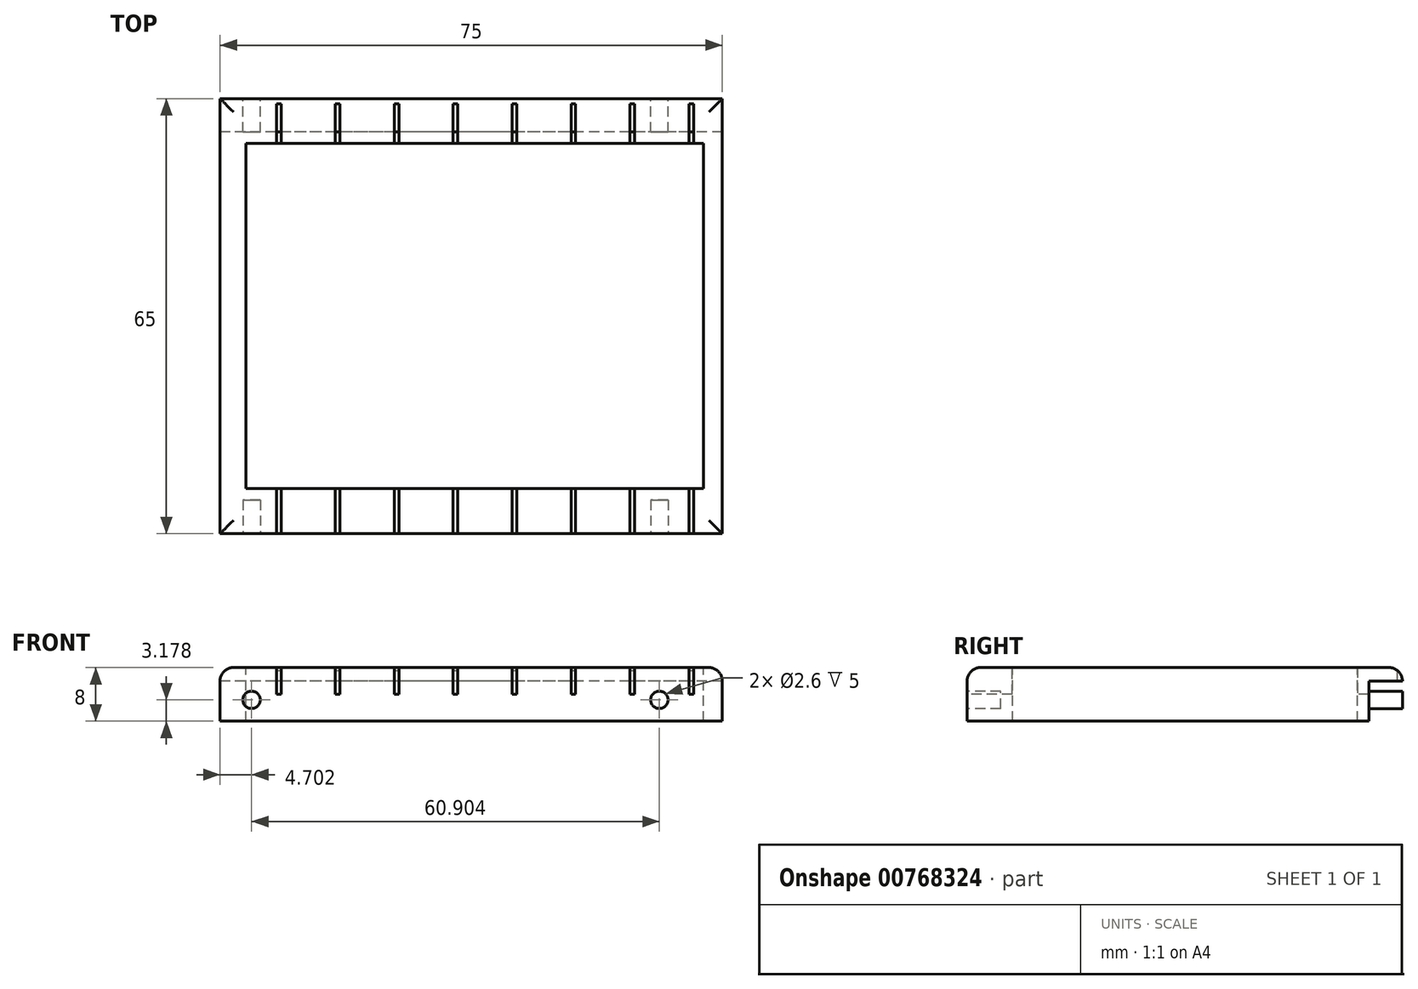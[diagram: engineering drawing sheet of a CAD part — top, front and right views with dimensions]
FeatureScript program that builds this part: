
annotation { "Feature Type Name" : "Feature", "Feature Type Description" : "" }
export const myFeature = defineFeature(function(context is Context, id is Id, definition is map)
    precondition{}
    {
        {
            var Q0;
            Q0=qCreatedBy(makeId("Top.planeOp"),FACE);
            var sketch = newSketch(context, id + "F0", { "sketchPlane" : qUnion([Q0])});
            skLineSegment(sketch, "E0.bottom", {"start": v(37.5, -32.5) * mm, "end": v(-37.5, -32.5) * mm});
            skLineSegment(sketch, "E0.top", {"start": v(37.5, 32.5) * mm, "end": v(-37.5, 32.5) * mm});
            skLineSegment(sketch, "E0.left", {"start": v(37.5, -32.5) * mm, "end": v(37.5, 32.5) * mm});
            skLineSegment(sketch, "E0.right", {"start": v(-37.5, -32.5) * mm, "end": v(-37.5, 32.5) * mm});
            skPoint(sketch, "E0.middle", {"position": v(0, 0) * mm});
            skSolve(sketch);
        }
        {
            var Q0;
            Q0=makeQuery(id+"F0.imprint","IMPRINT",FACE,{"disambiguationData":[TD([[makeQuery(id+"F0.imprint","IMPRINT",EDGE,{"derivedFrom":sQuery(id+"F0.wireOp",EDGE,"E0.bottom")}),-1.0]])]});
            extrude(context, id + "F1", {"entities" : qUnion([Q0]), "depth" : 8 * mm, "offsetDistance" : 25 * mm});
        }
        {
            var Q0;
            Q0=makeQuery(id+"F1.opExtrude","CAP_FACE",FACE,{"disambiguationData":[OSD([sQuery(id+"F0.wireOp",EDGE,"E0.bottom"),sQuery(id+"F0.wireOp",EDGE,"E0.top"),sQuery(id+"F0.wireOp",EDGE,"E0.left"),sQuery(id+"F0.wireOp",EDGE,"E0.right")])],"isStart":false});
            fillet(context, id + "F2", {"entities" : qUnion([Q0]), "radius" : 2 * mm, "tangentPropagation" : true, "allowEdgeOverflow" : false});
        }
        {
            var Q0;
            Q0=makeQuery(id+"F1.opExtrude","CAP_FACE",FACE,{"disambiguationData":[OSD([sQuery(id+"F0.wireOp",EDGE,"E0.bottom"),sQuery(id+"F0.wireOp",EDGE,"E0.top"),sQuery(id+"F0.wireOp",EDGE,"E0.left"),sQuery(id+"F0.wireOp",EDGE,"E0.right")])],"isStart":false});
            var sketch = newSketch(context, id + "F3", { "sketchPlane" : qUnion([Q0])});
            skLineSegment(sketch, "E1.bottom", {"start": v(-33.66, 25.81) * mm, "end": v(34.67, 25.81) * mm});
            skLineSegment(sketch, "E1.top", {"start": v(-33.66, -25.73) * mm, "end": v(34.67, -25.73) * mm});
            skLineSegment(sketch, "E1.left", {"start": v(-33.66, 25.81) * mm, "end": v(-33.66, -25.73) * mm});
            skLineSegment(sketch, "E1.right", {"start": v(34.67, 25.81) * mm, "end": v(34.67, -25.73) * mm});
            skSolve(sketch);
        }
        {
            var Q0;
            Q0=makeQuery(id+"F3.imprint","IMPRINT",FACE,{"disambiguationData":[TD([[makeQuery(id+"F3.imprint","IMPRINT",EDGE,{"derivedFrom":sQuery(id+"F3.wireOp",EDGE,"E1.bottom")}),-1.0]])]});
            extrude(context, id + "F4", {"entities" : qUnion([Q0]), "operationType" : NewBodyOperationType.REMOVE, "endBound" : BoundingType.THROUGH_ALL, "oppositeDirection" : true, "depth" : 25 * mm, "offsetDistance" : 25 * mm});
        }
        {
            var Q0;
            Q0=makeQuery(id+"F1.opExtrude","CAP_FACE",FACE,{"disambiguationData":[OSD([sQuery(id+"F0.wireOp",EDGE,"E0.bottom"),sQuery(id+"F0.wireOp",EDGE,"E0.top"),sQuery(id+"F0.wireOp",EDGE,"E0.left"),sQuery(id+"F0.wireOp",EDGE,"E0.right")])],"isStart":false});
            var sketch = newSketch(context, id + "F5", { "sketchPlane" : qUnion([Q0])});
            skLineSegment(sketch, "E2.bottom", {"start": v(-29.09, 31.73) * mm, "end": v(-28.39, 31.73) * mm});
            skLineSegment(sketch, "E2.top", {"start": v(-29.09, 24.23) * mm, "end": v(-28.39, 24.23) * mm});
            skLineSegment(sketch, "E2.left", {"start": v(-29.09, 31.73) * mm, "end": v(-29.09, 24.23) * mm});
            skLineSegment(sketch, "E2.right", {"start": v(-28.39, 31.73) * mm, "end": v(-28.39, 24.23) * mm});
            skLineSegment(sketch, "E3.bottom", {"start": v(-28.39, -25.77) * mm, "end": v(-29.09, -25.77) * mm});
            skLineSegment(sketch, "E3.top", {"start": v(-28.39, -33.27) * mm, "end": v(-29.09, -33.27) * mm});
            skLineSegment(sketch, "E3.left", {"start": v(-28.39, -25.77) * mm, "end": v(-28.39, -33.27) * mm});
            skLineSegment(sketch, "E3.right", {"start": v(-29.09, -25.77) * mm, "end": v(-29.09, -33.27) * mm});
            skLineSegment(sketch, "E4.1.0.0", {"start": v(-19.59, 31.73) * mm, "end": v(-19.59, 24.23) * mm});
            skLineSegment(sketch, "E4.1.0.1", {"start": v(-20.29, 31.73) * mm, "end": v(-19.59, 31.73) * mm});
            skLineSegment(sketch, "E4.1.0.2", {"start": v(-20.29, 31.73) * mm, "end": v(-20.29, 24.23) * mm});
            skLineSegment(sketch, "E4.1.0.3", {"start": v(-20.29, 24.23) * mm, "end": v(-19.59, 24.23) * mm});
            skLineSegment(sketch, "E4.1.0.4", {"start": v(-19.59, -25.77) * mm, "end": v(-19.59, -33.27) * mm});
            skLineSegment(sketch, "E4.1.0.5", {"start": v(-19.59, -25.77) * mm, "end": v(-20.29, -25.77) * mm});
            skLineSegment(sketch, "E4.1.0.6", {"start": v(-20.29, -25.77) * mm, "end": v(-20.29, -33.27) * mm});
            skLineSegment(sketch, "E4.1.0.7", {"start": v(-19.59, -33.27) * mm, "end": v(-20.29, -33.27) * mm});
            skLineSegment(sketch, "E4.2.0.0", {"start": v(-10.79, 31.73) * mm, "end": v(-10.79, 24.23) * mm});
            skLineSegment(sketch, "E4.2.0.1", {"start": v(-11.49, 31.73) * mm, "end": v(-10.79, 31.73) * mm});
            skLineSegment(sketch, "E4.2.0.2", {"start": v(-11.49, 31.73) * mm, "end": v(-11.49, 24.23) * mm});
            skLineSegment(sketch, "E4.2.0.3", {"start": v(-11.49, 24.23) * mm, "end": v(-10.79, 24.23) * mm});
            skLineSegment(sketch, "E4.2.0.4", {"start": v(-10.79, -25.77) * mm, "end": v(-10.79, -33.27) * mm});
            skLineSegment(sketch, "E4.2.0.5", {"start": v(-10.79, -25.77) * mm, "end": v(-11.49, -25.77) * mm});
            skLineSegment(sketch, "E4.2.0.6", {"start": v(-11.49, -25.77) * mm, "end": v(-11.49, -33.27) * mm});
            skLineSegment(sketch, "E4.2.0.7", {"start": v(-10.79, -33.27) * mm, "end": v(-11.49, -33.27) * mm});
            skLineSegment(sketch, "E4.3.0.0", {"start": v(-1.99, 31.73) * mm, "end": v(-1.99, 24.23) * mm});
            skLineSegment(sketch, "E4.3.0.1", {"start": v(-2.69, 31.73) * mm, "end": v(-1.99, 31.73) * mm});
            skLineSegment(sketch, "E4.3.0.2", {"start": v(-2.69, 31.73) * mm, "end": v(-2.69, 24.23) * mm});
            skLineSegment(sketch, "E4.3.0.3", {"start": v(-2.69, 24.23) * mm, "end": v(-1.99, 24.23) * mm});
            skLineSegment(sketch, "E4.3.0.4", {"start": v(-1.99, -25.77) * mm, "end": v(-1.99, -33.27) * mm});
            skLineSegment(sketch, "E4.3.0.5", {"start": v(-1.99, -25.77) * mm, "end": v(-2.69, -25.77) * mm});
            skLineSegment(sketch, "E4.3.0.6", {"start": v(-2.69, -25.77) * mm, "end": v(-2.69, -33.27) * mm});
            skLineSegment(sketch, "E4.3.0.7", {"start": v(-1.99, -33.27) * mm, "end": v(-2.69, -33.27) * mm});
            skLineSegment(sketch, "E4.4.0.0", {"start": v(6.81, 31.73) * mm, "end": v(6.81, 24.23) * mm});
            skLineSegment(sketch, "E4.4.0.1", {"start": v(6.11, 31.73) * mm, "end": v(6.81, 31.73) * mm});
            skLineSegment(sketch, "E4.4.0.2", {"start": v(6.11, 31.73) * mm, "end": v(6.11, 24.23) * mm});
            skLineSegment(sketch, "E4.4.0.3", {"start": v(6.11, 24.23) * mm, "end": v(6.81, 24.23) * mm});
            skLineSegment(sketch, "E4.4.0.4", {"start": v(6.81, -25.77) * mm, "end": v(6.81, -33.27) * mm});
            skLineSegment(sketch, "E4.4.0.5", {"start": v(6.81, -25.77) * mm, "end": v(6.11, -25.77) * mm});
            skLineSegment(sketch, "E4.4.0.6", {"start": v(6.11, -25.77) * mm, "end": v(6.11, -33.27) * mm});
            skLineSegment(sketch, "E4.4.0.7", {"start": v(6.81, -33.27) * mm, "end": v(6.11, -33.27) * mm});
            skLineSegment(sketch, "E4.5.0.0", {"start": v(15.61, 31.73) * mm, "end": v(15.61, 24.23) * mm});
            skLineSegment(sketch, "E4.5.0.1", {"start": v(14.91, 31.73) * mm, "end": v(15.61, 31.73) * mm});
            skLineSegment(sketch, "E4.5.0.2", {"start": v(14.91, 31.73) * mm, "end": v(14.91, 24.23) * mm});
            skLineSegment(sketch, "E4.5.0.3", {"start": v(14.91, 24.23) * mm, "end": v(15.61, 24.23) * mm});
            skLineSegment(sketch, "E4.5.0.4", {"start": v(15.61, -25.77) * mm, "end": v(15.61, -33.27) * mm});
            skLineSegment(sketch, "E4.5.0.5", {"start": v(15.61, -25.77) * mm, "end": v(14.91, -25.77) * mm});
            skLineSegment(sketch, "E4.5.0.6", {"start": v(14.91, -25.77) * mm, "end": v(14.91, -33.27) * mm});
            skLineSegment(sketch, "E4.5.0.7", {"start": v(15.61, -33.27) * mm, "end": v(14.91, -33.27) * mm});
            skLineSegment(sketch, "E4.6.0.0", {"start": v(24.41, 31.73) * mm, "end": v(24.41, 24.23) * mm});
            skLineSegment(sketch, "E4.6.0.1", {"start": v(23.71, 31.73) * mm, "end": v(24.41, 31.73) * mm});
            skLineSegment(sketch, "E4.6.0.2", {"start": v(23.71, 31.73) * mm, "end": v(23.71, 24.23) * mm});
            skLineSegment(sketch, "E4.6.0.3", {"start": v(23.71, 24.23) * mm, "end": v(24.41, 24.23) * mm});
            skLineSegment(sketch, "E4.6.0.4", {"start": v(24.41, -25.77) * mm, "end": v(24.41, -33.27) * mm});
            skLineSegment(sketch, "E4.6.0.5", {"start": v(24.41, -25.77) * mm, "end": v(23.71, -25.77) * mm});
            skLineSegment(sketch, "E4.6.0.6", {"start": v(23.71, -25.77) * mm, "end": v(23.71, -33.27) * mm});
            skLineSegment(sketch, "E4.6.0.7", {"start": v(24.41, -33.27) * mm, "end": v(23.71, -33.27) * mm});
            skLineSegment(sketch, "E4.7.0.0", {"start": v(33.21, 31.73) * mm, "end": v(33.21, 24.23) * mm});
            skLineSegment(sketch, "E4.7.0.1", {"start": v(32.51, 31.73) * mm, "end": v(33.21, 31.73) * mm});
            skLineSegment(sketch, "E4.7.0.2", {"start": v(32.51, 31.73) * mm, "end": v(32.51, 24.23) * mm});
            skLineSegment(sketch, "E4.7.0.3", {"start": v(32.51, 24.23) * mm, "end": v(33.21, 24.23) * mm});
            skLineSegment(sketch, "E4.7.0.4", {"start": v(33.21, -25.77) * mm, "end": v(33.21, -33.27) * mm});
            skLineSegment(sketch, "E4.7.0.5", {"start": v(33.21, -25.77) * mm, "end": v(32.51, -25.77) * mm});
            skLineSegment(sketch, "E4.7.0.6", {"start": v(32.51, -25.77) * mm, "end": v(32.51, -33.27) * mm});
            skLineSegment(sketch, "E4.7.0.7", {"start": v(33.21, -33.27) * mm, "end": v(32.51, -33.27) * mm});
            skLineSegment(sketch, "E4.direction1", {"start": v(-28.39, 24.23) * mm, "end": v(-19.59, 24.23) * mm, "construction": true});
            skSolve(sketch);
        }
        {
            var Q0;
            Q0 = qSketchRegion(id + "F5", true);
            extrude(context, id + "F6", {"entities" : qUnion([Q0]), "operationType" : NewBodyOperationType.REMOVE, "oppositeDirection" : true, "depth" : 4 * mm, "offsetDistance" : 25 * mm});
        }
        {
            var Q0;
            Q0=makeQuery(id+"F1.opExtrude","SWEPT_FACE",FACE,{"disambiguationData":[OSD([sQuery(id+"F0.wireOp",EDGE,"E0.bottom")])]});
            var sketch = newSketch(context, id + "F7", { "sketchPlane" : qUnion([Q0])});
            skCircle(sketch, "E5", {"center": v(28.1, 3.18) * mm, "radius": 1.3 * mm});
            skCircle(sketch, "E6", {"center": v(-32.8, 3.18) * mm, "radius": 1.3 * mm});
            skSolve(sketch);
        }
        {
            var Q0;
            Q0=makeQuery(id+"F1.opExtrude","SWEPT_FACE",FACE,{"disambiguationData":[OSD([sQuery(id+"F0.wireOp",EDGE,"E0.top")])]});
            var sketch = newSketch(context, id + "F8", { "sketchPlane" : qUnion([Q0])});
            skCircle(sketch, "E7.0", {"center": v(-28.1, 3.18) * mm, "radius": 1.3 * mm});
            skCircle(sketch, "E8.0", {"center": v(32.8, 3.18) * mm, "radius": 1.3 * mm});
            skSolve(sketch);
        }
        {
            var Q0;
            Q0=makeQuery(id+"F7.imprint","IMPRINT",FACE,{"disambiguationData":[TD([[makeQuery(id+"F7.imprint","IMPRINT",EDGE,{"derivedFrom":sQuery(id+"F7.wireOp",EDGE,"E6")}),1.0]])]});
            var Q1;
            Q1=makeQuery(id+"F7.imprint","IMPRINT",FACE,{"disambiguationData":[TD([[makeQuery(id+"F7.imprint","IMPRINT",EDGE,{"derivedFrom":sQuery(id+"F7.wireOp",EDGE,"E5")}),1.0]])]});
            var Q2;
            Q2=sQuery(id+"F7.wireOp",EDGE,"E6");
            var Q3;
            Q3=sQuery(id+"F7.wireOp",EDGE,"E5");
            extrude(context, id + "F9", {"entities" : qUnion([Q0, Q1]), "operationType" : NewBodyOperationType.REMOVE, "surfaceEntities" : qUnion([Q2, Q3]), "oppositeDirection" : true, "depth" : 5 * mm, "offsetDistance" : 25 * mm});
        }
        {
            var Q0;
            Q0=makeQuery(id+"F8.imprint","IMPRINT",FACE,{"disambiguationData":[TD([[makeQuery(id+"F8.imprint","IMPRINT",EDGE,{"derivedFrom":sQuery(id+"F8.wireOp",EDGE,"E8.0")}),-1.0]])]});
            var Q1;
            Q1=makeQuery(id+"F8.imprint","IMPRINT",FACE,{"disambiguationData":[TD([[makeQuery(id+"F8.imprint","IMPRINT",EDGE,{"derivedFrom":sQuery(id+"F8.wireOp",EDGE,"E7.0")}),-1.0]])]});
            var Q2;
            Q2=sQuery(id+"F8.wireOp",EDGE,"E8.0");
            extrude(context, id + "F10", {"entities" : qUnion([Q0, Q1]), "operationType" : NewBodyOperationType.REMOVE, "surfaceEntities" : qUnion([Q2]), "oppositeDirection" : true, "depth" : 5 * mm, "offsetDistance" : 25 * mm});
        }
    });
